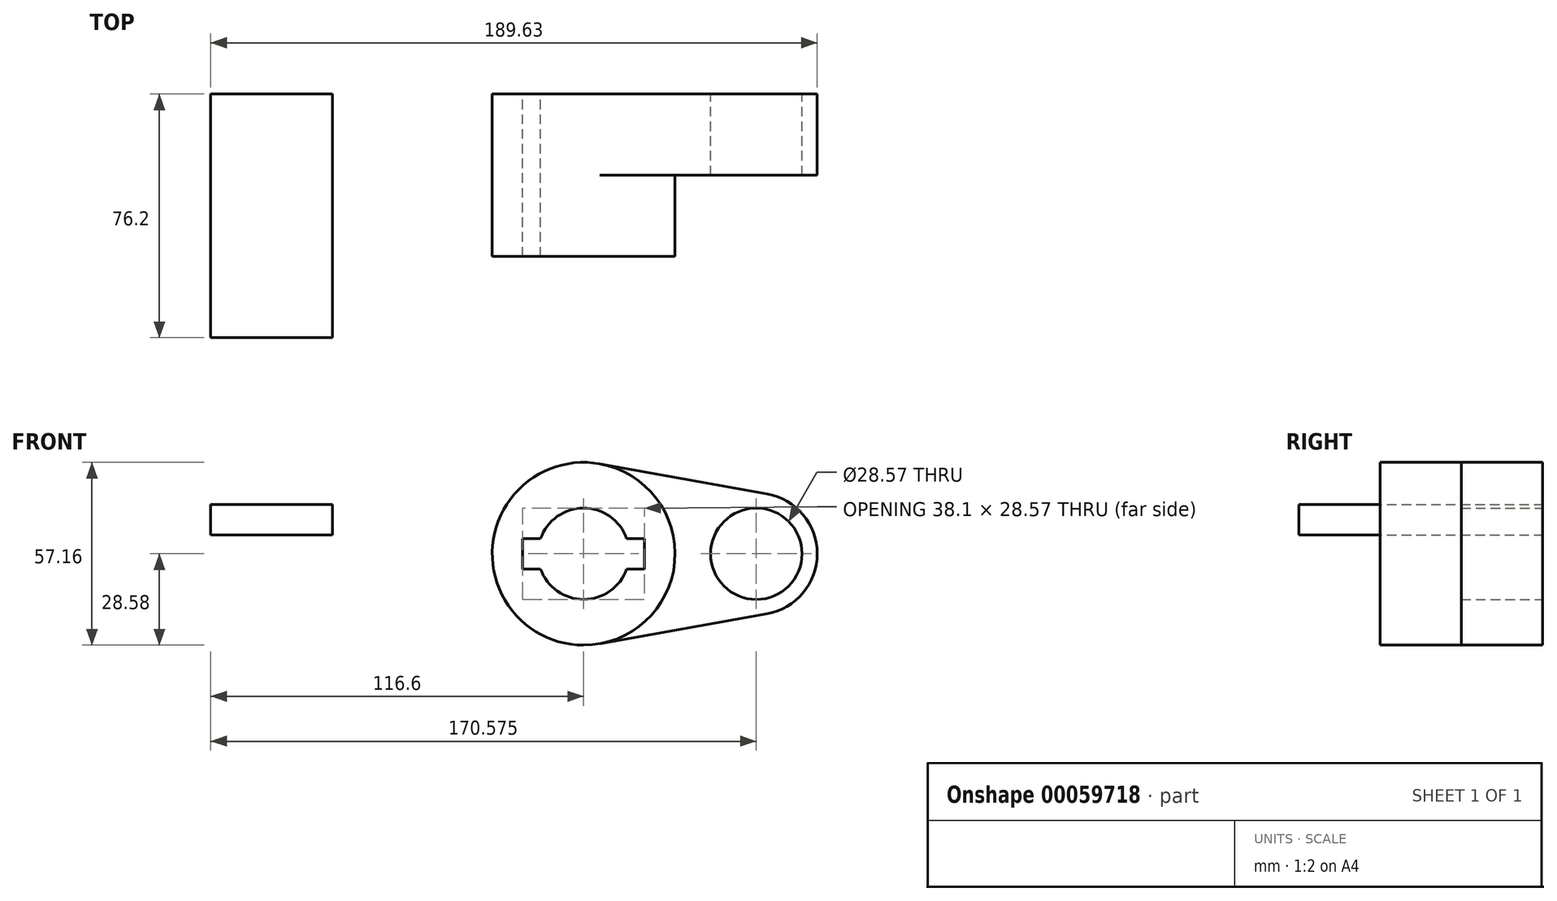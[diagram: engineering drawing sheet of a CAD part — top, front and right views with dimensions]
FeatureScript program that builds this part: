
annotation { "Feature Type Name" : "Feature", "Feature Type Description" : "" }
export const myFeature = defineFeature(function(context is Context, id is Id, definition is map)
    precondition{}
    {
        {
            var Q0;
            Q0=qCreatedBy(makeId("Front.planeOp"),FACE);
            var sketch = newSketch(context, id + "F0", { "sketchPlane" : qUnion([Q0])});
            skCircle(sketch, "E0", {"center": v(0, 0) * mm, "radius": 28.58 * mm});
            skCircle(sketch, "E1", {"center": v(53.98, 0) * mm, "radius": 19.06 * mm});
            skLineSegment(sketch, "E2", {"start": v(5.04, 28.13) * mm, "end": v(57.34, 18.76) * mm});
            skLineSegment(sketch, "E3", {"start": v(5.04, -28.13) * mm, "end": v(57.34, -18.76) * mm});
            skCircle(sketch, "E4", {"center": v(0, 0) * mm, "radius": 14.29 * mm});
            skCircle(sketch, "E5", {"center": v(53.98, 0) * mm, "radius": 14.29 * mm});
            skLineSegment(sketch, "E6.rect.bottom", {"start": v(19.05, -4.76) * mm, "end": v(-19.05, -4.76) * mm});
            skLineSegment(sketch, "E6.rect.top", {"start": v(19.05, 4.76) * mm, "end": v(-19.05, 4.76) * mm});
            skLineSegment(sketch, "E6.rect.left", {"start": v(19.05, -4.76) * mm, "end": v(19.05, 4.76) * mm});
            skLineSegment(sketch, "E6.rect.right", {"start": v(-19.05, -4.76) * mm, "end": v(-19.05, 4.76) * mm});
            skSolve(sketch);
        }
        {
            var Q0;
            {var subQ11=sQuery(id+"F0.wireOp",EDGE,"E6.rect.left");Q0=makeQuery(id+"F0.imprint","IMPRINT",FACE,{"disambiguationData":[TD([[makeQuery(id+"F0.imprint","IMPRINT",EDGE,{"derivedFrom":subQ11}),-1.0]])]});}
            var Q1;
            {var subQ0=sQuery(id+"F0.wireOp",EDGE,"E2");Q1=makeQuery(id+"F0.imprint","IMPRINT",FACE,{"disambiguationData":[TD([[makeQuery(id+"F0.imprint","IMPRINT",EDGE,{"derivedFrom":subQ0}),-1.0]])]});}
            var Q2;
            Q2=makeQuery(id+"F0.imprint","IMPRINT",FACE,{"disambiguationData":[TD([[makeQuery(id+"F0.imprint","IMPRINT",EDGE,{"derivedFrom":sQuery(id+"F0.wireOp",EDGE,"E5")}),-1.0]])]});
            extrude(context, id + "F1", {"entities" : qUnion([Q0, Q1, Q2]), "depth" : 25.4 * mm});
        }
        {
            var Q0;
            {var subQ11=sQuery(id+"F0.wireOp",EDGE,"E6.rect.left");Q0=makeQuery(id+"F0.imprint","IMPRINT",FACE,{"disambiguationData":[TD([[makeQuery(id+"F0.imprint","IMPRINT",EDGE,{"derivedFrom":subQ11}),-1.0]])]});}
            extrude(context, id + "F2", {"entities" : qUnion([Q0]), "operationType" : NewBodyOperationType.ADD, "depth" : 50.8 * mm});
        }
        {
            var Q0;
            Q0=qCreatedBy(makeId("Front.planeOp"),FACE);
            var sketch = newSketch(context, id + "F3", { "sketchPlane" : qUnion([Q0])});
            skLineSegment(sketch, "E7.bottom", {"start": v(-116.6, 15.46) * mm, "end": v(-78.5, 15.46) * mm});
            skLineSegment(sketch, "E7.top", {"start": v(-116.6, 5.93) * mm, "end": v(-78.5, 5.93) * mm});
            skLineSegment(sketch, "E7.left", {"start": v(-116.6, 15.46) * mm, "end": v(-116.6, 5.93) * mm});
            skLineSegment(sketch, "E7.right", {"start": v(-78.5, 15.46) * mm, "end": v(-78.5, 5.93) * mm});
            skSolve(sketch);
        }
        {
            var Q0;
            Q0 = qSketchRegion(id + "F3", true);
            extrude(context, id + "F4", {"entities" : qUnion([Q0]), "depth" : 76.2 * mm});
        }
    });
